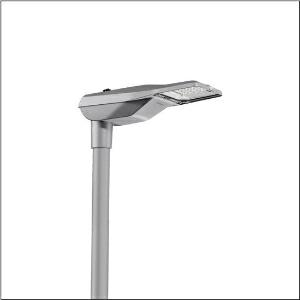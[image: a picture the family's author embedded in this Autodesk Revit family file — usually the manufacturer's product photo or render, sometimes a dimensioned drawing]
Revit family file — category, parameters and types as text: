
# Revit family: streetlight_sl_21_iq_micro___st1_0ab_5xe1m31v08cb_08ed
name_source: partatom
category: Lighting Fixtures
units: mm (PartAtom-declared; Revit-internal decimal feet)

## family parameters
Cut with Voids When Loaded = No
Host = Face
Light Source = No
Part Type = Normal
Room Calculation Point = No
Round Connector Dimension = Use Diameter
Shared = No

## types (1)
- --- (1 x LED, 2530 lm, 19.1 W, 3000K)
    Apparent Load = 19 VA
    CIE Flux Codes = 38 73 97 100 100
    Color Rendering = 70
    Color Temperature = 3000K
    Default Elevation = 1800 mm
    Description = Streetlight SL 21 iQ micro, mast luminaire, primary light control with lens, of PMMA, primary optical cover: cover, of toughened safety glass, transparent, light distribution: ST1.0aB, light emission: direct distribution, primary light characteristic: asymmetric, installation type: post-top, side-entry, LED, High Power LED, rated luminous flux: 2.530lm, luminous efficacy: 133lm/W, light colour: 730, colour temperature: 3000K, control: presetting dimming logarithmic, Street-Remote, Auto-Match, Temp-Guard, Lumen-Switch, Night-Set, Smart-Wire, Light-Fading, Desk-Remote (wireless, voltage-free reading and setting of iQ features in the workshop via application-optimized NFC function/RFID function), optimised constant luminous flux control (CLO 2.0), mains connection: 220..240V, AC, 50/60Hz, start of lifetime: 19W, end of service life: 20W, reduction: 9W, luminaire housing, of diecast aluminium, powder-coated, Siteco® metallic grey (DB 702S), corrosivity category C5 mid according to DIN EN ISO 12944, please order mast flange separately, inclination adjustable: 0°, 5°, 10°, 15°, sealing non-destructively replaceable, multi-level sealing system, length: 528mm, width: 235mm, height: 110mm, mast flange for spigot size: 42mm (side-entry): 5XC10008XM4, 60/48mm (side-entry/post-top): 5XC10108XM2, 76/60mm (side-entry/post-top): 5XC10108XM1, Smart Interface above, protection rating (complete): IP66, insulation class (complete): insulation class II (safety insulation), certification: CE, ENEC, ENEC+, VDE, impact resistance: IK09, permissible operating ambient temperature for outdoor applications: -40..+50°C, standard-compliant lighting for roads and squares, packaging unit: 1 piece

Light Distribution: ST1.0aB
    Height = 110 mm
    Lamp = 1 x LED
    Lamp Light Flux = 2530 lm
    Lamp Power = 19.1 W
    Lamp count = 1
    Length = 528 mm
    Luminous efficacy = 132 lm/W
    Manufacturer = Siteco
    ModVariant = No
    Model = 5XE1M31V08CB
    Number of Poles = 1
    OnlyDefault = Yes
    Power Factor = 1
    Product Name = Streetlight SL 21 iQ micro | ST1.0aB
    Product group = mast luminaire | pylon top
    ProductGroupID = 6100
    Protection Class = Protection class II
    Protection Degree = IP 66
    RLX_Detail_Level = 1
    RLX_Emergency_Light_Flux = 0 lm
    RLX_Emergency_Type = 0
    RLX_Emergency_Type_DB = No
    RlxData = <blob elided: 98421 chars, md5=85539f52>
    Socket = socket
    Standby Power = 0 W
    System Light Flux = 2530 lm
    System Power = 19 W
    Type Comments = factory setting: luminous flux: 100 % | dim-lin: 254 | 387 mA
    Type Image = l_1277292.jpg
    URL = http://relux.com
    VarID = @adj_042831
    Voltage = 0 V
    Weight = 0.00 kg
    Width = 235 mm

## geometry (parser evidence)
native form markers: Blend x4, Sweep x10
no freeform markers — native parametric forms only
